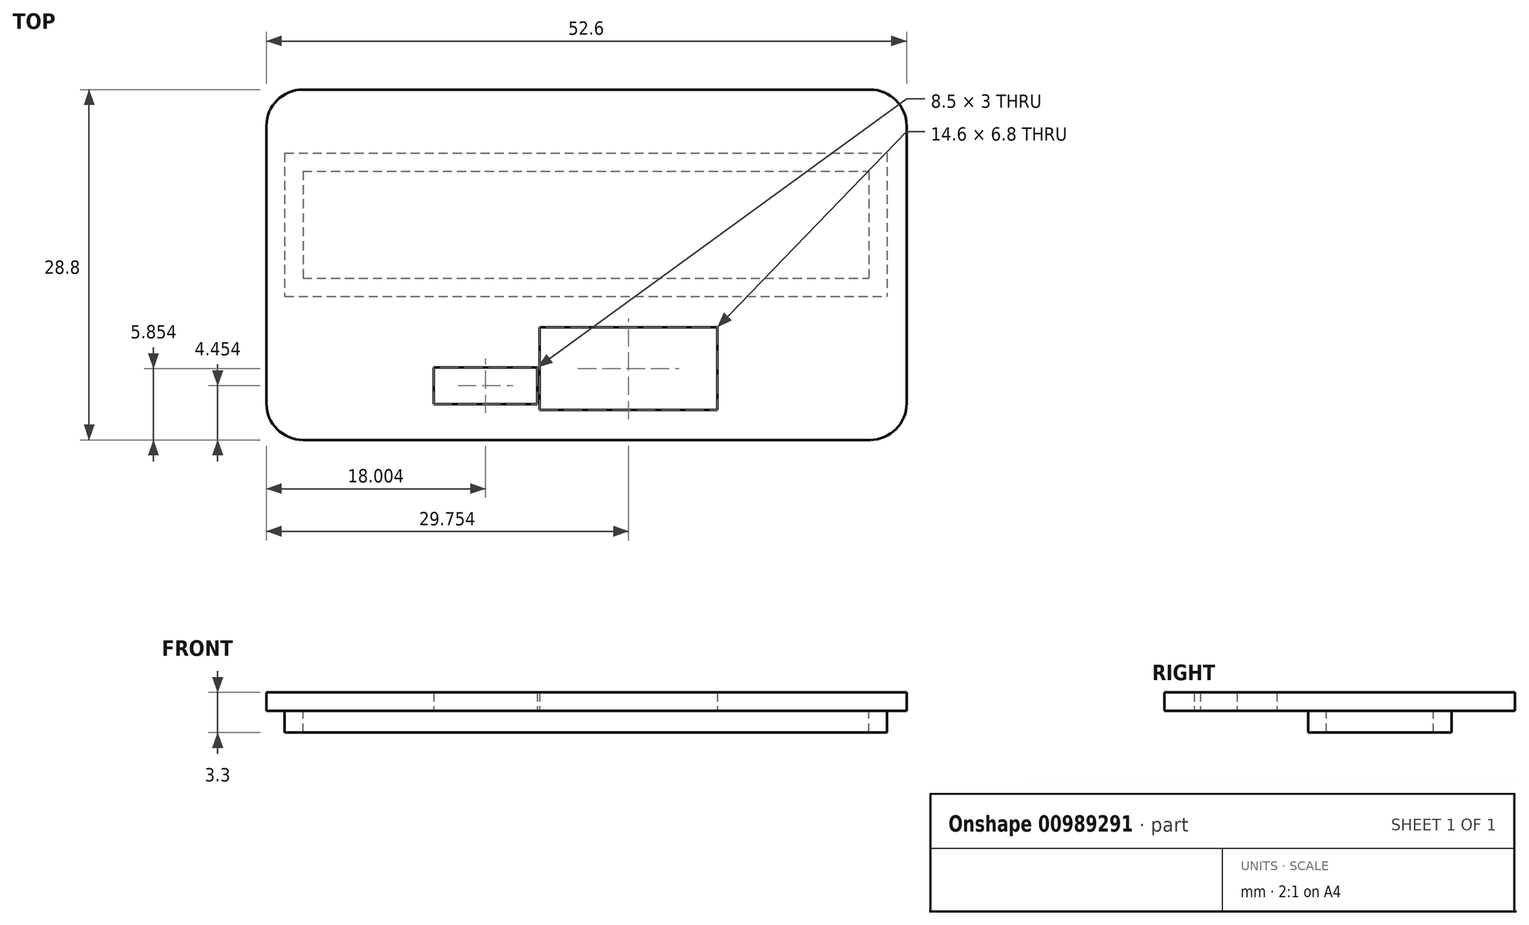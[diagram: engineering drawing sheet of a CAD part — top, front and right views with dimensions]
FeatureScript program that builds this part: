
annotation { "Feature Type Name" : "Feature", "Feature Type Description" : "" }
export const myFeature = defineFeature(function(context is Context, id is Id, definition is map)
    precondition{}
    {
        {
            var Q0;
            Q0=qCreatedBy(makeId("Top.planeOp"),FACE);
            var sketch = newSketch(context, id + "F0", { "sketchPlane" : qUnion([Q0])});
            skLineSegment(sketch, "E0.bottom", {"start": v(-29.16, 20.68) * mm, "end": v(23.44, 20.68) * mm});
            skLineSegment(sketch, "E0.top", {"start": v(-29.16, -8.12) * mm, "end": v(23.44, -8.12) * mm});
            skLineSegment(sketch, "E0.left", {"start": v(-29.16, 20.68) * mm, "end": v(-29.16, -8.12) * mm});
            skLineSegment(sketch, "E0.right", {"start": v(23.44, 20.68) * mm, "end": v(23.44, -8.12) * mm});
            skLineSegment(sketch, "E1.bottom", {"start": v(-27.66, 15.47) * mm, "end": v(21.84, 15.47) * mm});
            skLineSegment(sketch, "E1.top", {"start": v(-27.66, 3.67) * mm, "end": v(21.84, 3.67) * mm});
            skLineSegment(sketch, "E1.left", {"start": v(-27.66, 15.47) * mm, "end": v(-27.66, 3.67) * mm});
            skLineSegment(sketch, "E1.right", {"start": v(21.84, 15.47) * mm, "end": v(21.84, 3.67) * mm});
            skLineSegment(sketch, "E2.bottom", {"start": v(-26.66, 18.9) * mm, "end": v(21.34, 18.9) * mm});
            skLineSegment(sketch, "E2.top", {"start": v(-26.66, 16.37) * mm, "end": v(21.34, 16.37) * mm});
            skLineSegment(sketch, "E2.left", {"start": v(-26.66, 18.9) * mm, "end": v(-26.66, 16.37) * mm});
            skLineSegment(sketch, "E2.right", {"start": v(21.34, 18.9) * mm, "end": v(21.34, 16.37) * mm});
            skLineSegment(sketch, "E3", {"start": v(-22, -3.47) * mm, "end": v(-22, 1.23) * mm});
            skLineSegment(sketch, "E4", {"start": v(-22, 1.23) * mm, "end": v(20.9, 1.23) * mm});
            skLineSegment(sketch, "E5", {"start": v(20.9, 1.23) * mm, "end": v(20.9, -4.75) * mm});
            skLineSegment(sketch, "E6", {"start": v(20.9, -4.75) * mm, "end": v(20.9, -4.75) * mm});
            skLineSegment(sketch, "E7", {"start": v(20.9, -4.75) * mm, "end": v(20.9, -5.88) * mm});
            skLineSegment(sketch, "E8", {"start": v(20.9, -6.07) * mm, "end": v(-26.6, -6.07) * mm});
            skLineSegment(sketch, "E9", {"start": v(-26.6, -6.07) * mm, "end": v(-26.6, -5.27) * mm});
            skLineSegment(sketch, "E10", {"start": v(-26.6, -3.47) * mm, "end": v(-22, -3.47) * mm});
            skLineSegment(sketch, "E11.bottom", {"start": v(-6.7, 1.13) * mm, "end": v(7.9, 1.13) * mm});
            skLineSegment(sketch, "E11.top", {"start": v(-6.7, -5.67) * mm, "end": v(7.9, -5.67) * mm});
            skLineSegment(sketch, "E11.left", {"start": v(-6.7, 1.13) * mm, "end": v(-6.7, -5.67) * mm});
            skLineSegment(sketch, "E11.right", {"start": v(7.9, 1.13) * mm, "end": v(7.9, -5.67) * mm});
            skLineSegment(sketch, "E12.bottom", {"start": v(-15.4, -2.17) * mm, "end": v(-6.9, -2.17) * mm});
            skLineSegment(sketch, "E12.top", {"start": v(-15.4, -5.17) * mm, "end": v(-6.9, -5.17) * mm});
            skLineSegment(sketch, "E12.left", {"start": v(-15.4, -2.17) * mm, "end": v(-15.4, -5.17) * mm});
            skLineSegment(sketch, "E12.right", {"start": v(-6.9, -2.17) * mm, "end": v(-6.9, -5.17) * mm});
            skPoint(sketch, "E13", {"position": v(-6.9, -5.67) * mm});
            skLineSegment(sketch, "E14.0", {"start": v(-26.16, 13.97) * mm, "end": v(20.34, 13.97) * mm});
            skLineSegment(sketch, "E14.1", {"start": v(-26.16, 13.97) * mm, "end": v(-26.16, 5.17) * mm});
            skLineSegment(sketch, "E14.2", {"start": v(-26.16, 5.17) * mm, "end": v(20.34, 5.17) * mm});
            skLineSegment(sketch, "E14.3", {"start": v(20.34, 13.97) * mm, "end": v(20.34, 5.17) * mm});
            skLineSegment(sketch, "E15.0", {"start": v(21.9, -5.27) * mm, "end": v(-25.6, -5.27) * mm});
            skLineSegment(sketch, "E16", {"start": v(-26.6, -5.27) * mm, "end": v(-26.6, -3.47) * mm});
            skLineSegment(sketch, "E17", {"start": v(20.9, -5.27) * mm, "end": v(20.9, -6.07) * mm});
            skLineSegment(sketch, "E18", {"start": v(20.9, -5.27) * mm, "end": v(20.9, -5.88) * mm});
            skLineSegment(sketch, "E19.0", {"start": v(-26.5, -5.97) * mm, "end": v(-26.5, -5.37) * mm});
            skLineSegment(sketch, "E19.1", {"start": v(20.8, -5.97) * mm, "end": v(-26.5, -5.97) * mm});
            skLineSegment(sketch, "E19.2", {"start": v(20.8, -5.37) * mm, "end": v(20.8, -5.97) * mm});
            skLineSegment(sketch, "E19.3", {"start": v(20.8, -5.37) * mm, "end": v(-26.5, -5.37) * mm});
            skLineSegment(sketch, "E20.0", {"start": v(-25.86, 18.1) * mm, "end": v(-25.86, 17.17) * mm});
            skLineSegment(sketch, "E20.1", {"start": v(-25.86, 18.1) * mm, "end": v(20.54, 18.1) * mm});
            skLineSegment(sketch, "E20.2", {"start": v(20.54, 18.1) * mm, "end": v(20.54, 17.17) * mm});
            skLineSegment(sketch, "E20.3", {"start": v(-25.86, 17.17) * mm, "end": v(20.54, 17.17) * mm});
            skSolve(sketch);
        }
        {
            var Q0;
            Q0=makeQuery(id+"F0.imprint","IMPRINT",FACE,{"disambiguationData":[TD([[makeQuery(id+"F0.imprint","IMPRINT",EDGE,{"derivedFrom":sQuery(id+"F0.wireOp",EDGE,"E2.bottom")}),-1.0]])]});
            var Q1;
            Q1=makeQuery(id+"F0.imprint","IMPRINT",FACE,{"disambiguationData":[TD([[makeQuery(id+"F0.imprint","IMPRINT",EDGE,{"derivedFrom":sQuery(id+"F0.wireOp",EDGE,"E0.bottom")}),-1.0]])]});
            var Q2;
            Q2=makeQuery(id+"F0.imprint","IMPRINT",FACE,{"disambiguationData":[TD([[makeQuery(id+"F0.imprint","IMPRINT",EDGE,{"derivedFrom":sQuery(id+"F0.wireOp",EDGE,"E1.bottom")}),-1.0]])]});
            var Q3;
            Q3=makeQuery(id+"F0.imprint","IMPRINT",FACE,{"disambiguationData":[TD([[makeQuery(id+"F0.imprint","IMPRINT",EDGE,{"derivedFrom":sQuery(id+"F0.wireOp",EDGE,"E3")}),-1.0]])]});
            var Q4;
            Q4=makeQuery(id+"F0.imprint","IMPRINT",FACE,{"disambiguationData":[TD([[makeQuery(id+"F0.imprint","IMPRINT",EDGE,{"derivedFrom":sQuery(id+"F0.wireOp",EDGE,"E14.0")}),-1.0]])]});
            var Q5;
            Q5=makeQuery(id+"F0.imprint","IMPRINT",FACE,{"disambiguationData":[TD([[makeQuery(id+"F0.imprint","IMPRINT",EDGE,{"derivedFrom":sQuery(id+"F0.wireOp",EDGE,"E3")}),-1.0]])]});
            var Q6;
            {var subQ2=sQuery(id+"F0.wireOp",EDGE,"E11.top");Q6=makeQuery(id+"F0.imprint","IMPRINT",FACE,{"disambiguationData":[TD([[makeQuery(id+"F0.imprint","IMPRINT",EDGE,{"derivedFrom":subQ2}),-1.0]])]});}
            var Q7;
            Q7=makeQuery(id+"F0.imprint","IMPRINT",FACE,{"disambiguationData":[TD([[makeQuery(id+"F0.imprint","IMPRINT",EDGE,{"derivedFrom":sQuery(id+"F0.wireOp",EDGE,"E20.0")}),1.0]])]});
            extrude(context, id + "F1", {"entities" : qUnion([Q0, Q1, Q2, Q3, Q4, Q5, Q6, Q7]), "depth" : 1.5 * mm, "offsetDistance" : 25 * mm});
        }
        {
            var Q0;
            Q0=makeQuery(id+"F0.imprint","IMPRINT",FACE,{"disambiguationData":[TD([[makeQuery(id+"F0.imprint","IMPRINT",EDGE,{"derivedFrom":sQuery(id+"F0.wireOp",EDGE,"E1.bottom")}),-1.0]])]});
            extrude(context, id + "F2", {"entities" : qUnion([Q0]), "operationType" : NewBodyOperationType.ADD, "oppositeDirection" : true, "depth" : 1.8 * mm, "offsetDistance" : 25 * mm});
        }
        {
            var Q0;
            Q0=makeQuery(id+"F1.opExtrude","SWEPT_EDGE",EDGE,{"disambiguationData":[OSD([sQuery(id+"F0.wireOp",EDGE,"E0.top"),sQuery(id+"F0.wireOp",EDGE,"E0.right")])]});
            var Q1;
            Q1=makeQuery(id+"F1.opExtrude","SWEPT_EDGE",EDGE,{"disambiguationData":[OSD([sQuery(id+"F0.wireOp",EDGE,"E0.bottom"),sQuery(id+"F0.wireOp",EDGE,"E0.right")])]});
            var Q2;
            Q2=makeQuery(id+"F1.opExtrude","SWEPT_EDGE",EDGE,{"disambiguationData":[OSD([sQuery(id+"F0.wireOp",EDGE,"E0.bottom"),sQuery(id+"F0.wireOp",EDGE,"E0.left")])]});
            var Q3;
            Q3=makeQuery(id+"F1.opExtrude","SWEPT_EDGE",EDGE,{"disambiguationData":[OSD([sQuery(id+"F0.wireOp",EDGE,"E0.top"),sQuery(id+"F0.wireOp",EDGE,"E0.left")])]});
            fillet(context, id + "F3", {"entities" : qUnion([Q0, Q1, Q2, Q3]), "radius" : 3 * mm, "tangentPropagation" : true, "allowEdgeOverflow" : false});
        }
    });
